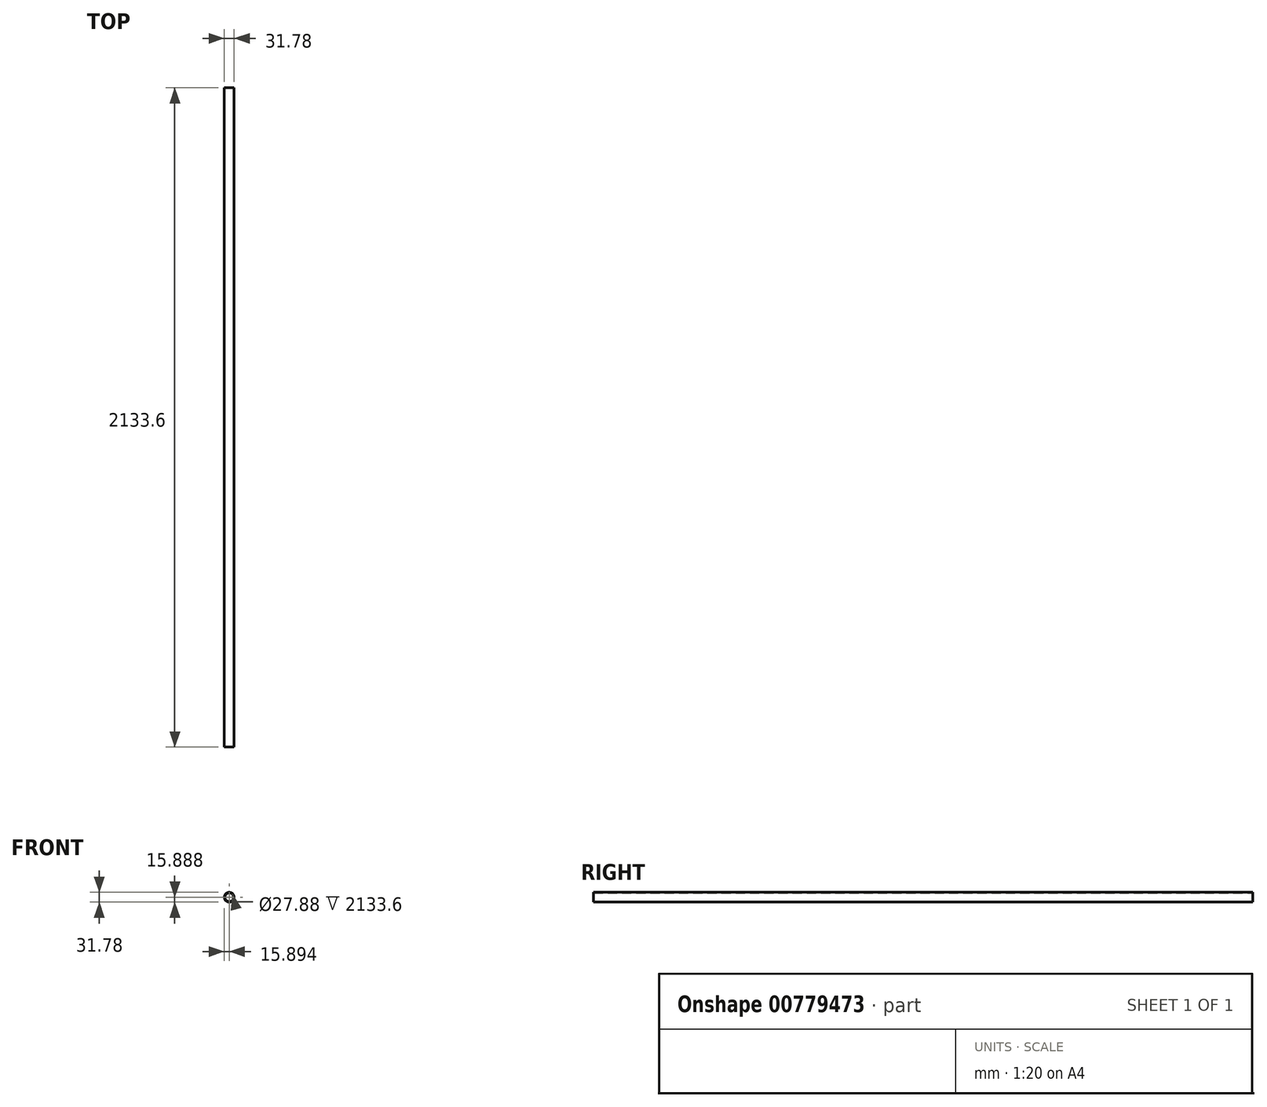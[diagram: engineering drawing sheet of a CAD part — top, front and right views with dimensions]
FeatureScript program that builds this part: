
annotation { "Feature Type Name" : "Feature", "Feature Type Description" : "" }
export const myFeature = defineFeature(function(context is Context, id is Id, definition is map)
    precondition{}
    {
        {
            var Q0;
            Q0=qCreatedBy(makeId("Front.planeOp"),FACE);
            var sketch = newSketch(context, id + "F0", { "sketchPlane" : qUnion([Q0])});
            skLineSegment(sketch, "E0.right", {"start": v(2104.4, 0) * mm, "end": v(2104.4, -31.32) * mm});
            skCircle(sketch, "E1", {"center": v(29.92, -15.88) * mm, "radius": 15.9 * mm});
            skPoint(sketch, "E1.first.point", {"position": v(30.42, 0) * mm});
            skPoint(sketch, "E1.second.point", {"position": v(29.08, -31.75) * mm});
            skPoint(sketch, "E1.third.point", {"position": v(45.8, -15.16) * mm});
            skCircle(sketch, "E2", {"center": v(29.92, -15.88) * mm, "radius": 13.94 * mm});
            skSolve(sketch);
        }
        {
            var Q0;
            Q0=makeQuery(id+"F0.imprint","IMPRINT",FACE,{"disambiguationData":[TD([[makeQuery(id+"F0.imprint","IMPRINT",EDGE,{"derivedFrom":sQuery(id+"F0.wireOp",EDGE,"E1")}),1.0]])]});
            extrude(context, id + "F1", {"entities" : qUnion([Q0]), "endBound" : BoundingType.SYMMETRIC, "depth" : 2133.6 * mm, "offsetDistance" : 25.4 * mm});
        }
    });
